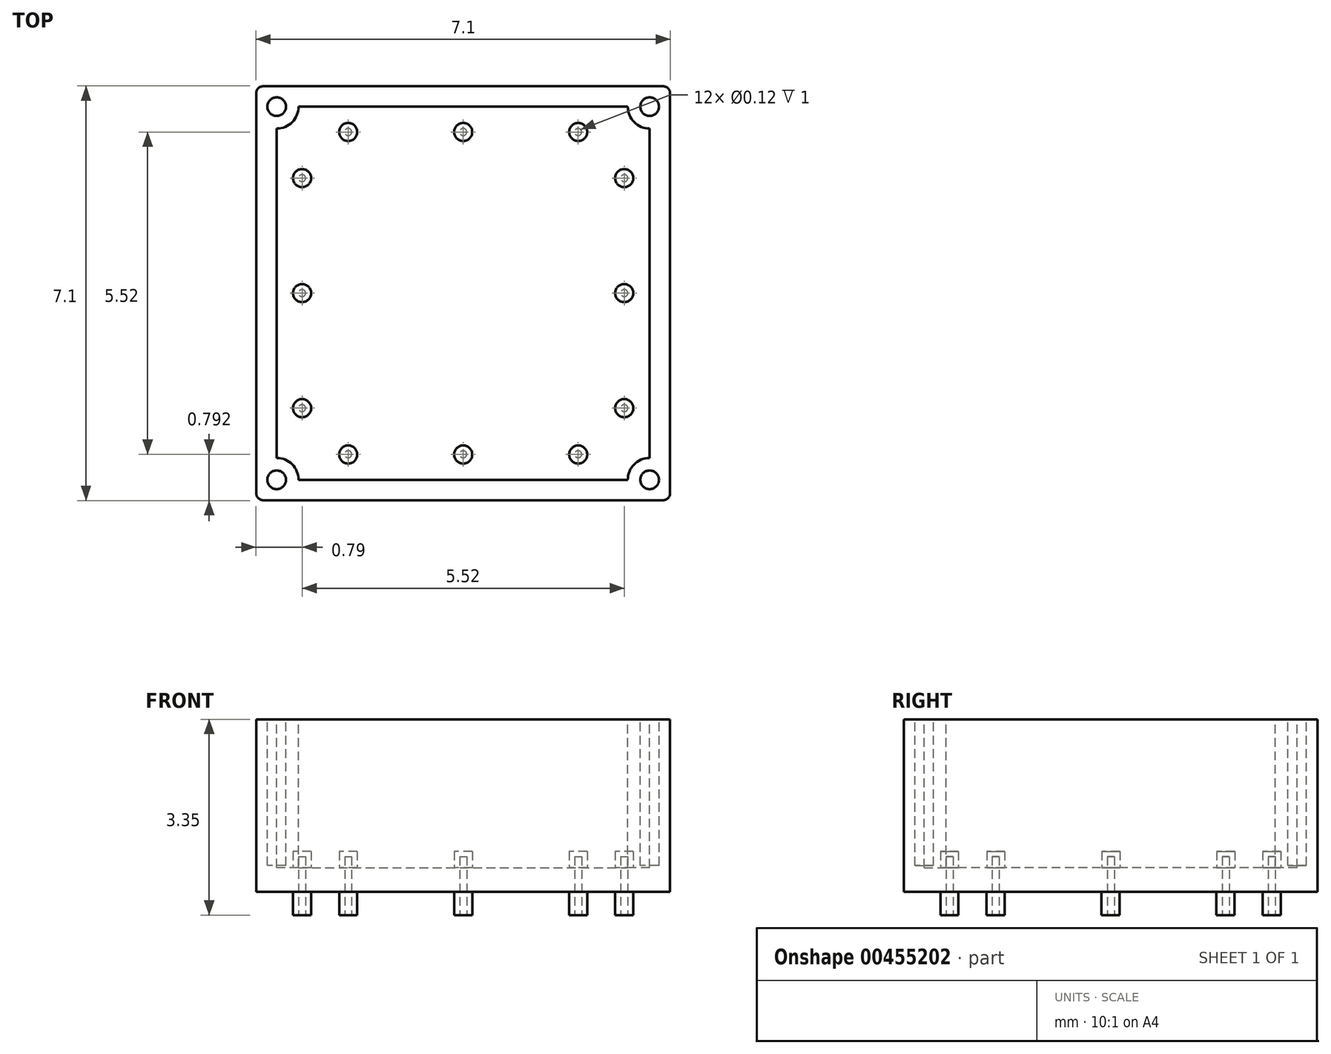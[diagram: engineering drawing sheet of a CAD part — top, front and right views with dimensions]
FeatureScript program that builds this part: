
annotation { "Feature Type Name" : "Feature", "Feature Type Description" : "" }
export const myFeature = defineFeature(function(context is Context, id is Id, definition is map)
    precondition{}
    {
        {
            var Q0;
            Q0=qCreatedBy(makeId("Top.planeOp"),FACE);
            var sketch = newSketch(context, id + "F0", { "sketchPlane" : qUnion([Q0])});
            skLineSegment(sketch, "E0.bottom", {"start": v(-3.54, 3.55) * mm, "end": v(3.54, 3.55) * mm});
            skLineSegment(sketch, "E0.top", {"start": v(-3.54, -3.54) * mm, "end": v(3.54, -3.54) * mm});
            skLineSegment(sketch, "E0.left", {"start": v(-3.55, 3.54) * mm, "end": v(-3.54, -3.54) * mm});
            skLineSegment(sketch, "E0.right", {"start": v(3.54, 3.54) * mm, "end": v(3.54, -3.54) * mm});
            skSolve(sketch);
        }
        {
            var Q0;
            Q0 = qSketchRegion(id + "F0", true);
            extrude(context, id + "F1", {"entities" : qUnion([Q0]), "depth" : 2.95 * mm});
        }
        {
            var Q0;
            Q0=makeQuery(id+"F1.opExtrude","CAP_FACE",FACE,{"disambiguationData":[OSD([sQuery(id+"F0.wireOp",EDGE,"E0.bottom"),sQuery(id+"F0.wireOp",EDGE,"E0.top"),sQuery(id+"F0.wireOp",EDGE,"E0.left"),sQuery(id+"F0.wireOp",EDGE,"E0.right")])],"isStart":false});
            var sketch = newSketch(context, id + "F2", { "sketchPlane" : qUnion([Q0])});
            skCircle(sketch, "E1", {"center": v(-3.2, 3.2) * mm, "radius": 0.16 * mm});
            skCircle(sketch, "E2.MirrorC", {"center": v(-3.2, -3.2) * mm, "radius": 0.16 * mm});
            skCircle(sketch, "E3.MirrorC", {"center": v(3.2, 3.2) * mm, "radius": 0.16 * mm});
            skCircle(sketch, "E4.MirrorC", {"center": v(3.2, -3.2) * mm, "radius": 0.16 * mm});
            skSolve(sketch);
        }
        {
            var Q0;
            Q0 = qSketchRegion(id + "F2", true);
            extrude(context, id + "F3", {"entities" : qUnion([Q0]), "operationType" : NewBodyOperationType.REMOVE, "oppositeDirection" : true, "depth" : 2.5 * mm});
        }
        {
            var Q0;
            Q0=makeQuery(id+"F1.opExtrude","CAP_FACE",FACE,{"disambiguationData":[OSD([sQuery(id+"F0.wireOp",EDGE,"E0.bottom"),sQuery(id+"F0.wireOp",EDGE,"E0.top"),sQuery(id+"F0.wireOp",EDGE,"E0.left"),sQuery(id+"F0.wireOp",EDGE,"E0.right")])],"isStart":false});
            var sketch = newSketch(context, id + "F4", { "sketchPlane" : qUnion([Q0])});
            skLineSegment(sketch, "E5.bottom", {"start": v(-2.82, 3.2) * mm, "end": v(2.82, 3.2) * mm});
            skLineSegment(sketch, "E5.top", {"start": v(-2.82, -3.2) * mm, "end": v(2.82, -3.2) * mm});
            skLineSegment(sketch, "E5.left", {"start": v(-3.2, 2.82) * mm, "end": v(-3.2, -2.82) * mm});
            skLineSegment(sketch, "E5.right", {"start": v(3.2, 2.82) * mm, "end": v(3.2, -2.82) * mm});
            skArc(sketch, "E6", {"start": v(3.2, -2.82) * mm, "mid": v(2.93, -2.93) * mm, "end": v(2.82, -3.2) * mm});
            skArc(sketch, "E7.MirrorCS", {"start": v(-3.2, -2.82) * mm, "mid": v(-2.93, -2.93) * mm, "end": v(-2.82, -3.2) * mm});
            skArc(sketch, "E8.MirrorCS", {"start": v(-3.2, 2.82) * mm, "mid": v(-2.93, 2.93) * mm, "end": v(-2.82, 3.2) * mm});
            skArc(sketch, "E9.MirrorCS", {"start": v(3.2, 2.82) * mm, "mid": v(2.93, 2.93) * mm, "end": v(2.82, 3.2) * mm});
            skSolve(sketch);
        }
        {
            var Q0;
            Q0 = qSketchRegion(id + "F4", true);
            extrude(context, id + "F5", {"entities" : qUnion([Q0]), "operationType" : NewBodyOperationType.REMOVE, "oppositeDirection" : true, "depth" : 2.54 * mm});
        }
        {
            var Q0;
            Q0=makeQuery(id+"F1.opExtrude","SWEPT_EDGE",EDGE,{"disambiguationData":[OSD([sQuery(id+"F0.wireOp",EDGE,"E0.top"),sQuery(id+"F0.wireOp",EDGE,"E0.left")])]});
            var Q1;
            Q1=makeQuery(id+"F1.opExtrude","SWEPT_EDGE",EDGE,{"disambiguationData":[OSD([sQuery(id+"F0.wireOp",EDGE,"E0.bottom"),sQuery(id+"F0.wireOp",EDGE,"E0.left")])]});
            var Q2;
            Q2=makeQuery(id+"F1.opExtrude","SWEPT_EDGE",EDGE,{"disambiguationData":[OSD([sQuery(id+"F0.wireOp",EDGE,"E0.bottom"),sQuery(id+"F0.wireOp",EDGE,"E0.right")])]});
            var Q3;
            Q3=makeQuery(id+"F1.opExtrude","SWEPT_EDGE",EDGE,{"disambiguationData":[OSD([sQuery(id+"F0.wireOp",EDGE,"E0.top"),sQuery(id+"F0.wireOp",EDGE,"E0.right")])]});
            fillet(context, id + "F6", {"entities" : qUnion([Q0, Q1, Q2, Q3]), "radius" : .12 * mm, "tangentPropagation" : true, "allowEdgeOverflow" : false});
        }
        {
            var Q0;
            Q0=makeQuery(id+"F1.opExtrude","CAP_FACE",FACE,{"disambiguationData":[OSD([sQuery(id+"F0.wireOp",EDGE,"E0.bottom"),sQuery(id+"F0.wireOp",EDGE,"E0.top"),sQuery(id+"F0.wireOp",EDGE,"E0.left"),sQuery(id+"F0.wireOp",EDGE,"E0.right")])],"isStart":true});
            var sketch = newSketch(context, id + "F7", { "sketchPlane" : qUnion([Q0])});
            skCircle(sketch, "E10", {"center": v(-1.97, 2.76) * mm, "radius": 0.15 * mm});
            skCircle(sketch, "E11", {"center": v(0, 2.76) * mm, "radius": 0.15 * mm});
            skCircle(sketch, "E12", {"center": v(-2.76, 1.97) * mm, "radius": 0.15 * mm});
            skCircle(sketch, "E13", {"center": v(1.97, 2.76) * mm, "radius": 0.15 * mm});
            skCircle(sketch, "E14", {"center": v(-2.76, 0) * mm, "radius": 0.15 * mm});
            skCircle(sketch, "E15", {"center": v(-2.76, -1.97) * mm, "radius": 0.15 * mm});
            skCircle(sketch, "E16.MirrorC", {"center": v(2.76, 1.97) * mm, "radius": 0.15 * mm});
            skCircle(sketch, "E17.MirrorC", {"center": v(2.76, 0) * mm, "radius": 0.15 * mm});
            skCircle(sketch, "E18.MirrorC", {"center": v(2.76, -1.97) * mm, "radius": 0.15 * mm});
            skCircle(sketch, "E19.MirrorC", {"center": v(-1.97, -2.76) * mm, "radius": 0.15 * mm});
            skCircle(sketch, "E20.MirrorC", {"center": v(0, -2.76) * mm, "radius": 0.15 * mm});
            skCircle(sketch, "E21.MirrorC", {"center": v(1.97, -2.76) * mm, "radius": 0.15 * mm});
            skSolve(sketch);
        }
        {
            var Q0;
            Q0 = qSketchRegion(id + "F7", true);
            extrude(context, id + "F8", {"entities" : qUnion([Q0]), "operationType" : NewBodyOperationType.ADD, "depth" : .4 * mm});
        }
        {
            var Q0;
            Q0=makeQuery(id+"F5.boolean.opBoolean","COPY",FACE,{"derivedFrom":makeQuery(id+"F5.opExtrude","CAP_FACE",FACE,{"disambiguationData":[OSD([sQuery(id+"F4.wireOp",EDGE,"E5.bottom"),sQuery(id+"F4.wireOp",EDGE,"E5.top"),sQuery(id+"F4.wireOp",EDGE,"E5.left"),sQuery(id+"F4.wireOp",EDGE,"E5.right"),sQuery(id+"F4.wireOp",EDGE,"E6"),sQuery(id+"F4.wireOp",EDGE,"E7.MirrorCS"),sQuery(id+"F4.wireOp",EDGE,"E8.MirrorCS"),sQuery(id+"F4.wireOp",EDGE,"E9.MirrorCS")])],"isStart":false})});
            var sketch = newSketch(context, id + "F9", { "sketchPlane" : qUnion([Q0])});
            skCircle(sketch, "E22", {"center": v(-1.97, 2.76) * mm, "radius": 0.15 * mm});
            skCircle(sketch, "E23", {"center": v(0, 2.76) * mm, "radius": 0.15 * mm});
            skCircle(sketch, "E24", {"center": v(1.97, 2.76) * mm, "radius": 0.15 * mm});
            skCircle(sketch, "E25", {"center": v(-2.76, 1.97) * mm, "radius": 0.15 * mm});
            skCircle(sketch, "E26", {"center": v(-2.76, 0) * mm, "radius": 0.15 * mm});
            skCircle(sketch, "E27", {"center": v(-2.76, -1.97) * mm, "radius": 0.15 * mm});
            skCircle(sketch, "E28.MirrorC", {"center": v(2.76, 1.97) * mm, "radius": 0.15 * mm});
            skCircle(sketch, "E29.MirrorC", {"center": v(2.76, 0) * mm, "radius": 0.15 * mm});
            skCircle(sketch, "E30.MirrorC", {"center": v(2.76, -1.97) * mm, "radius": 0.15 * mm});
            skCircle(sketch, "E31.MirrorC", {"center": v(-1.97, -2.76) * mm, "radius": 0.15 * mm});
            skCircle(sketch, "E32.MirrorC", {"center": v(0, -2.76) * mm, "radius": 0.15 * mm});
            skCircle(sketch, "E33.MirrorC", {"center": v(1.97, -2.76) * mm, "radius": 0.15 * mm});
            skSolve(sketch);
        }
        {
            var Q0;
            Q0 = qSketchRegion(id + "F9", true);
            extrude(context, id + "F10", {"entities" : qUnion([Q0]), "operationType" : NewBodyOperationType.ADD, "depth" : .28 * mm});
        }
        {
            var Q0;
            Q0=makeQuery(id+"F8.opExtrude","CAP_FACE",FACE,{"disambiguationData":[OSD([sQuery(id+"F7.wireOp",EDGE,"E10")])],"isStart":false});
            var sketch = newSketch(context, id + "F11", { "sketchPlane" : qUnion([Q0])});
            skCircle(sketch, "E34", {"center": v(-1.97, 2.76) * mm, "radius": 0.06 * mm});
            skCircle(sketch, "E35", {"center": v(-2.76, 1.97) * mm, "radius": 0.06 * mm});
            skCircle(sketch, "E36", {"center": v(0, 2.76) * mm, "radius": 0.06 * mm});
            skCircle(sketch, "E37", {"center": v(1.97, 2.76) * mm, "radius": 0.06 * mm});
            skCircle(sketch, "E38", {"center": v(2.76, 1.97) * mm, "radius": 0.06 * mm});
            skCircle(sketch, "E39", {"center": v(2.76, 0) * mm, "radius": 0.06 * mm});
            skCircle(sketch, "E40", {"center": v(-2.76, 0) * mm, "radius": 0.06 * mm});
            skCircle(sketch, "E41.MirrorC", {"center": v(-2.76, -1.97) * mm, "radius": 0.06 * mm});
            skCircle(sketch, "E42.MirrorC", {"center": v(-1.97, -2.76) * mm, "radius": 0.06 * mm});
            skCircle(sketch, "E43.MirrorC", {"center": v(0, -2.76) * mm, "radius": 0.06 * mm});
            skCircle(sketch, "E44.MirrorC", {"center": v(1.97, -2.76) * mm, "radius": 0.06 * mm});
            skCircle(sketch, "E45.MirrorC", {"center": v(2.76, -1.97) * mm, "radius": 0.06 * mm});
            skSolve(sketch);
        }
        {
            var Q0;
            Q0 = qSketchRegion(id + "F11", true);
            extrude(context, id + "F12", {"entities" : qUnion([Q0]), "operationType" : NewBodyOperationType.REMOVE, "oppositeDirection" : true, "depth" : 1 * mm});
        }
    });
